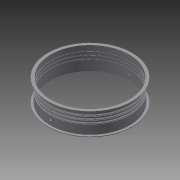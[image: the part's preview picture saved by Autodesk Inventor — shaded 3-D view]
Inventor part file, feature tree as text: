
AUTODESK INVENTOR PART (.ipt)
format: ipt  version: 2015 (Build 190159000, 159)  size: 441,856 bytes
history: native  units: in
note: dims shown in document units (in); Inventor stores cm internally (conversion verified against a paired STEP export)
features: sketch x3, extrude x2, revolve x1, plane x1
ambient origin geometry x8: Origin, YZ Plane, XZ Plane, XY Plane, X Axis, Y Axis, Z Axis, Center Point
bodies: Solid1 (feature_tree)
feature tree (7):
  revolve  "Revolution1"  [1 undecoded]
  extrude  "Extrusion1"  Depth=0.05in
  plane  "Work Plane1"
  extrude  "Extrusion2"  Depth=0.05in
  sketch  "Sketch1"  dims[d3=0.095in d21=0.05in]
  sketch  "Sketch2"  dims[d22=0.01in d23=0.05in]
  sketch  "Sketch3"  dims[d24=0.01in d25=0.05in d26=0.01in d27=0.025in d28=0.0in d56=0.025in d57=0.0in d58=0.89in d59=0.025in d60=0.0in d61=360.0deg d62=0.95in d63=0.95in d64=0.639in d65=22.8346in d67=360.0deg d69=1.0in d70=0.0in d78=0.03in d80=0.0in d106=1.0in d107=0.975in d108=0.925in d109=0.825in d110=0.725in d111=0.675in d112=0.5738in d113=0.525in d118=0.025in d120=1.875in d121=90.0deg d122=90.0deg d123=0.5in d124=0.045in d125=0.115in d126=0.095in d127=0.115in d128=0.125in d129=0.115in d130=0.095in d131=0.125in d132=0.095in d133=0.095in d134=0.2in d135=0.975in d136=0.425in d137=0.2in d138=0.25in d139=0.1in d140=1.0in d141=0.0in]
note: 1 required parameter value undecoded (feature->parameter linkage not recoverable at this tier; creation-order binding heuristic only, values carry confidence <= 0.55)
